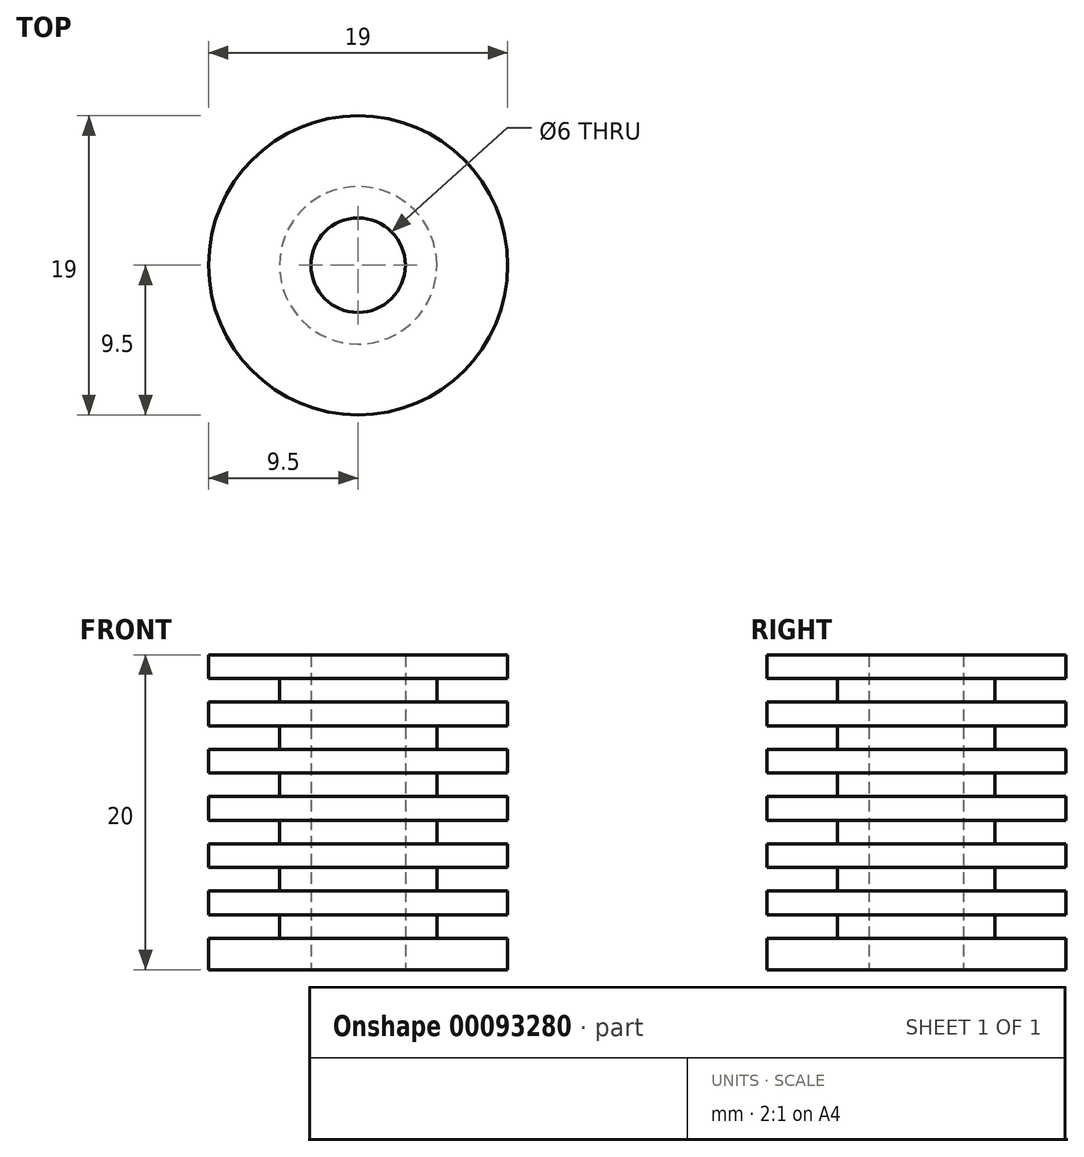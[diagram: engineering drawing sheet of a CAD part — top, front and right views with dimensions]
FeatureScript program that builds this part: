
annotation { "Feature Type Name" : "Feature", "Feature Type Description" : "" }
export const myFeature = defineFeature(function(context is Context, id is Id, definition is map)
    precondition{}
    {
        {
            var Q0;
            Q0=qCreatedBy(makeId("Top.planeOp"),FACE);
            var sketch = newSketch(context, id + "F0", { "sketchPlane" : qUnion([Q0])});
            skCircle(sketch, "E0", {"center": v(0, 0) * mm, "radius": 9.5 * mm});
            skCircle(sketch, "E1", {"center": v(0, 0) * mm, "radius": 3 * mm});
            skSolve(sketch);
        }
        {
            var Q0;
            Q0 = qSketchRegion(id + "F0", true);
            extrude(context, id + "F1", {"entities" : qUnion([Q0]), "depth" : 20 * mm});
        }
        {
            var Q0;
            Q0=qCreatedBy(makeId("Front.planeOp"),FACE);
            var sketch = newSketch(context, id + "F2", { "sketchPlane" : qUnion([Q0])});
            skLineSegment(sketch, "E2.bottom", {"start": v(-10, 18.5) * mm, "end": v(-5, 18.5) * mm});
            skLineSegment(sketch, "E2.top", {"start": v(-10, 17) * mm, "end": v(-5, 17) * mm});
            skLineSegment(sketch, "E2.left", {"start": v(-10, 18.5) * mm, "end": v(-10, 17) * mm});
            skLineSegment(sketch, "E2.right", {"start": v(-5, 18.5) * mm, "end": v(-5, 17) * mm});
            skLineSegment(sketch, "E3.0.1.0", {"start": v(-10, 15.5) * mm, "end": v(-5, 15.5) * mm});
            skLineSegment(sketch, "E3.0.1.1", {"start": v(-10, 14) * mm, "end": v(-5, 14) * mm});
            skLineSegment(sketch, "E3.0.1.2", {"start": v(-10, 15.5) * mm, "end": v(-10, 14) * mm});
            skLineSegment(sketch, "E3.0.1.3", {"start": v(-5, 15.5) * mm, "end": v(-5, 14) * mm});
            skLineSegment(sketch, "E3.0.2.0", {"start": v(-10, 12.5) * mm, "end": v(-5, 12.5) * mm});
            skLineSegment(sketch, "E3.0.2.1", {"start": v(-10, 11) * mm, "end": v(-5, 11) * mm});
            skLineSegment(sketch, "E3.0.2.2", {"start": v(-10, 12.5) * mm, "end": v(-10, 11) * mm});
            skLineSegment(sketch, "E3.0.2.3", {"start": v(-5, 12.5) * mm, "end": v(-5, 11) * mm});
            skLineSegment(sketch, "E3.0.3.0", {"start": v(-10, 9.5) * mm, "end": v(-5, 9.5) * mm});
            skLineSegment(sketch, "E3.0.3.1", {"start": v(-10, 8) * mm, "end": v(-5, 8) * mm});
            skLineSegment(sketch, "E3.0.3.2", {"start": v(-10, 9.5) * mm, "end": v(-10, 8) * mm});
            skLineSegment(sketch, "E3.0.3.3", {"start": v(-5, 9.5) * mm, "end": v(-5, 8) * mm});
            skLineSegment(sketch, "E3.0.4.0", {"start": v(-10, 6.5) * mm, "end": v(-5, 6.5) * mm});
            skLineSegment(sketch, "E3.0.4.1", {"start": v(-10, 5) * mm, "end": v(-5, 5) * mm});
            skLineSegment(sketch, "E3.0.4.2", {"start": v(-10, 6.5) * mm, "end": v(-10, 5) * mm});
            skLineSegment(sketch, "E3.0.4.3", {"start": v(-5, 6.5) * mm, "end": v(-5, 5) * mm});
            skLineSegment(sketch, "E3.0.5.0", {"start": v(-10, 3.5) * mm, "end": v(-5, 3.5) * mm});
            skLineSegment(sketch, "E3.0.5.1", {"start": v(-10, 2) * mm, "end": v(-5, 2) * mm});
            skLineSegment(sketch, "E3.0.5.2", {"start": v(-10, 3.5) * mm, "end": v(-10, 2) * mm});
            skLineSegment(sketch, "E3.0.5.3", {"start": v(-5, 3.5) * mm, "end": v(-5, 2) * mm});
            skLineSegment(sketch, "E3.direction1", {"start": v(-10, 18.5) * mm, "end": v(15.5, 18.5) * mm, "construction": true});
            skLineSegment(sketch, "E3.direction2", {"start": v(-10, 18.5) * mm, "end": v(-10, 15.5) * mm, "construction": true});
            skSolve(sketch);
        }
        {
            var Q0;
            Q0 = qSketchRegion(id + "F2", true);
            var Q1;
            Q1=makeQuery(id+"F1.opExtrude","CAP_EDGE",EDGE,{"disambiguationData":[OSD([sQuery(id+"F0.wireOp",EDGE,"E0")])],"isStart":false});
            revolve(context, id + "F3", {"operationType" : NewBodyOperationType.REMOVE, "entities" : qUnion([Q0]), "axis" : qUnion([Q1]), "revolveType" : RevolveType.FULL, "oppositeDirection" : true});
        }
    });
